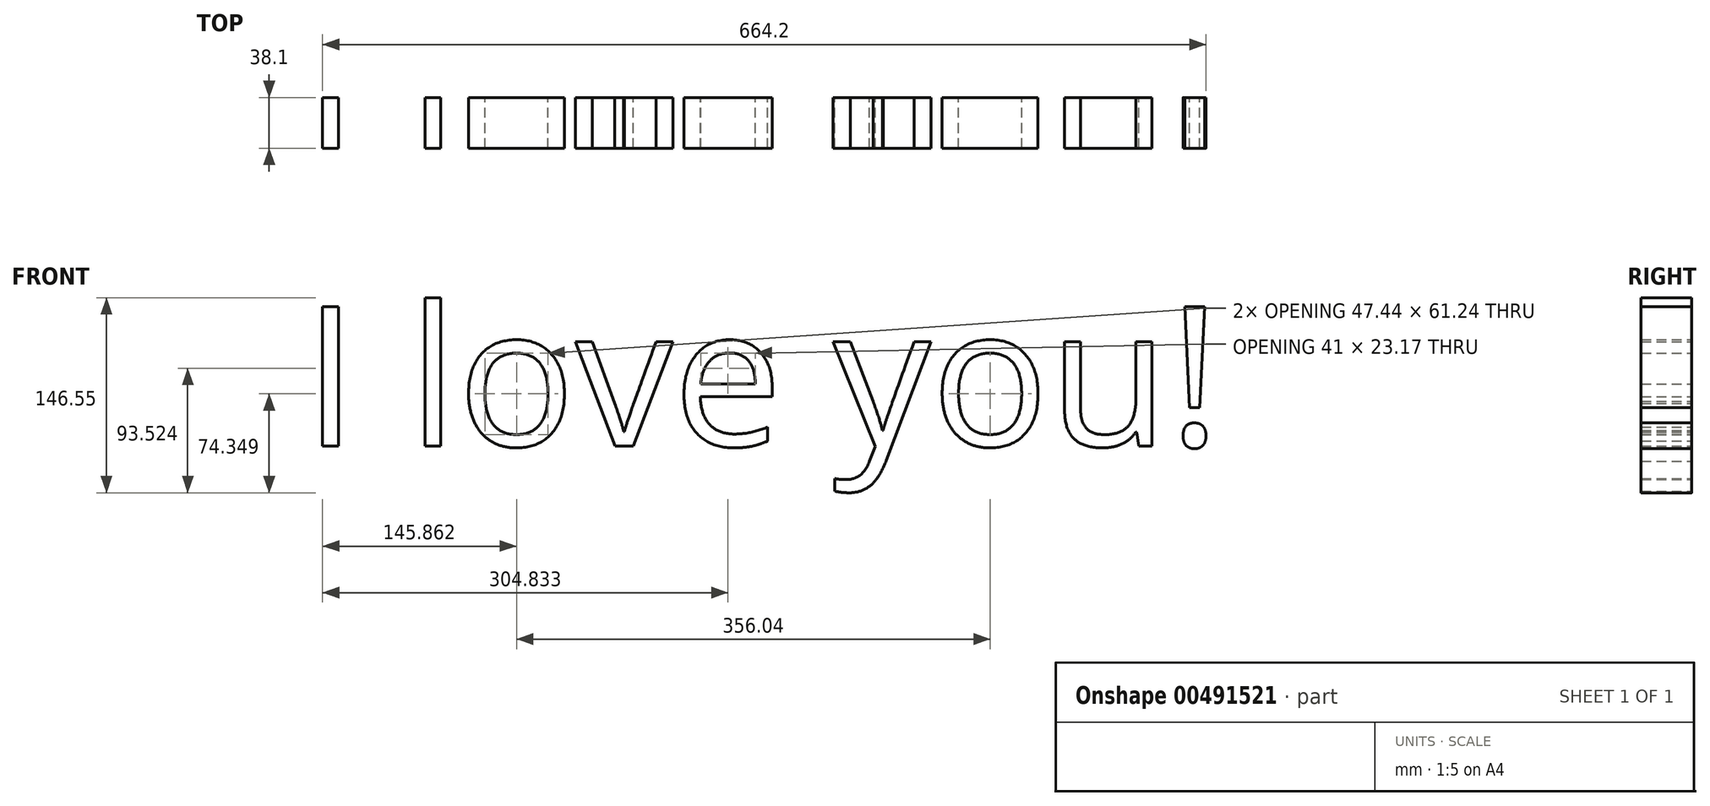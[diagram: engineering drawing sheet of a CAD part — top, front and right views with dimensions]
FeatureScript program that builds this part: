
annotation { "Feature Type Name" : "Feature", "Feature Type Description" : "" }
export const myFeature = defineFeature(function(context is Context, id is Id, definition is map)
    precondition{}
    {
        {
            var Q0;
            Q0=qCreatedBy(makeId("Front.planeOp"),FACE);
            var sketch = newSketch(context, id + "F0", { "sketchPlane" : qUnion([Q0])});
            skCircle(sketch, "E0.cCircle", {"center": v(59.76, 0) * mm, "radius": 67.17 * mm, "construction": true});
            skLineSegment(sketch, "E0.0", {"start": v(17.71, -65.18) * mm, "end": v(-17.71, 3.82) * mm});
            skLineSegment(sketch, "E0.1", {"start": v(-17.71, 3.82) * mm, "end": v(24.33, 69) * mm});
            skLineSegment(sketch, "E0.2", {"start": v(24.33, 69) * mm, "end": v(101.8, 65.18) * mm});
            skLineSegment(sketch, "E0.3", {"start": v(101.8, 65.18) * mm, "end": v(137.23, -3.82) * mm});
            skLineSegment(sketch, "E0.4", {"start": v(137.23, -3.82) * mm, "end": v(95.18, -69) * mm});
            skLineSegment(sketch, "E0.5", {"start": v(95.18, -69) * mm, "end": v(17.71, -65.18) * mm});
            skPoint(sketch, "E0.0.midPoint", {"position": v(0, -30.68) * mm});
            skSolve(sketch);
        }
        {
            var Q0;
            Q0 = qSketchRegion(id + "F0", true);
            var sketch = newSketch(context, id + "F1", { "sketchPlane" : qUnion([Q0])});
            skText(sketch, "E1", { "text": "I love you!", "fontName": "OpenSans-Regular.ttf"});
            const initialGuessF1  = {"E1": [-0.33925, -0.1055, 1, 0, 0.1055]};
            skSetInitialGuess(sketch, initialGuessF1);
            skSolve(sketch);
        }
        {
            var Q0;
            Q0 = qSketchRegion(id + "F1", true);
            var Q1;
            Q1 = qSketchRegion(id + "F1", true);
            extrude(context, id + "F2", {"entities" : qUnion([Q0]), "bodyType" : ToolBodyType.SURFACE, "surfaceEntities" : qUnion([Q1]), "depth" : 38.1 * mm});
        }
    });
